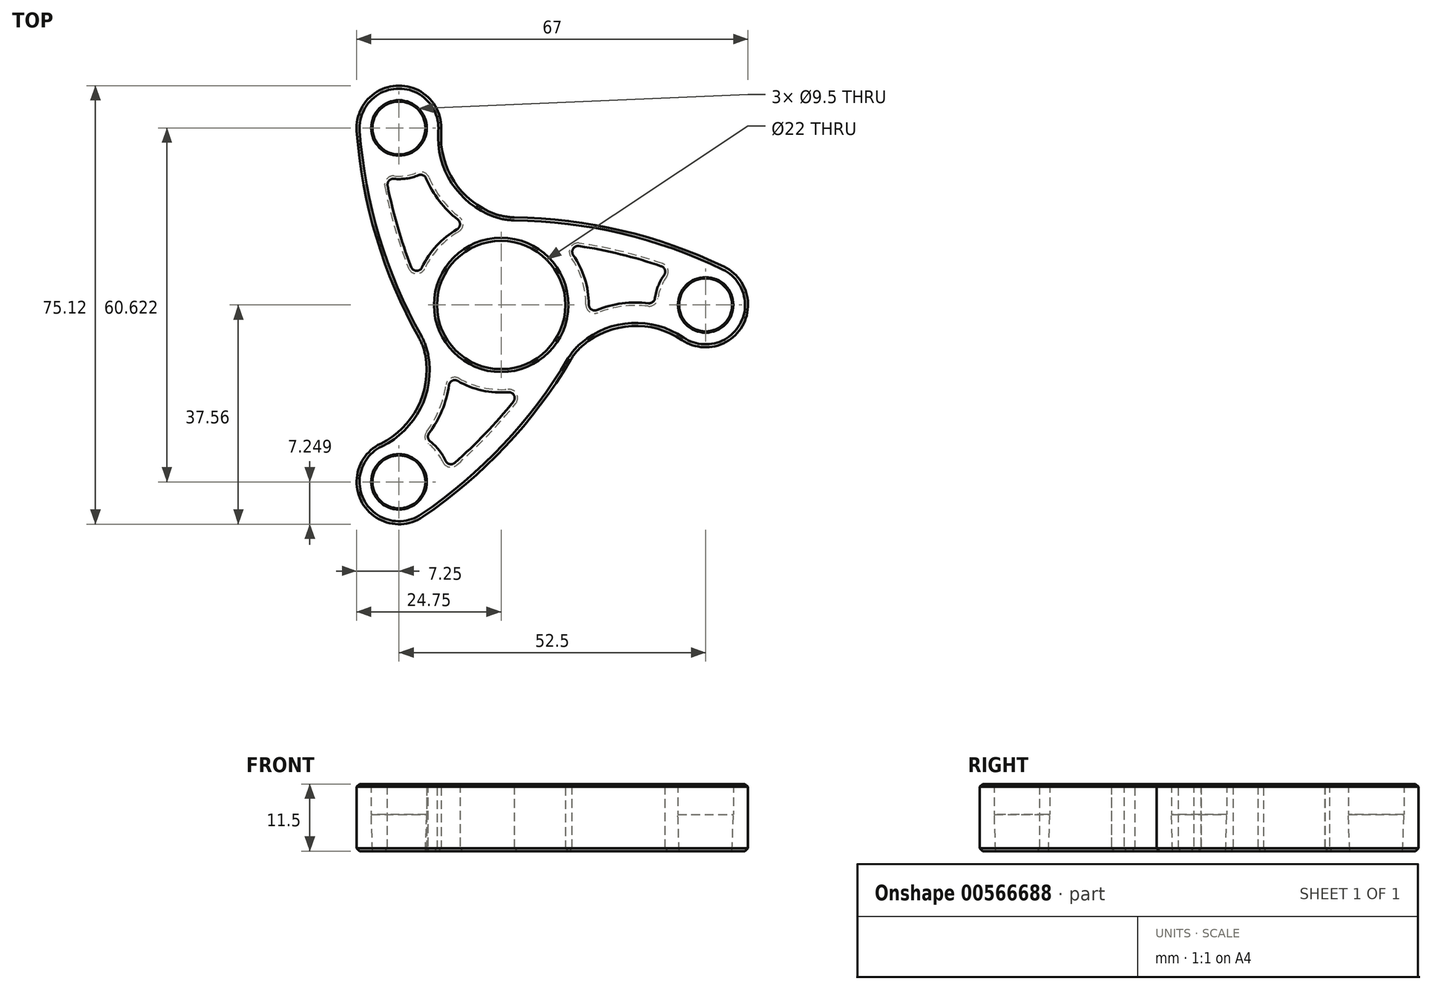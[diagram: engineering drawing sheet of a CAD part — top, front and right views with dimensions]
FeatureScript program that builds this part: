
annotation { "Feature Type Name" : "Feature", "Feature Type Description" : "" }
export const myFeature = defineFeature(function(context is Context, id is Id, definition is map)
    precondition{}
    {
        {
            var Q0;
            Q0=qCreatedBy(makeId("Top.planeOp"),FACE);
            var sketch = newSketch(context, id + "F0", { "sketchPlane" : qUnion([Q0])});
            skCircle(sketch, "E0", {"center": v(0, 0) * mm, "radius": 11 * mm});
            skArc(sketch, "E1.0", {"start": v(-0.24, 15) * mm, "mid": v(-13.39, -6.77) * mm, "end": v(11.93, -9.1) * mm});
            skLineSegment(sketch, "E2", {"start": v(0, 0) * mm, "end": v(35, 0) * mm, "construction": true});
            skArc(sketch, "E3", {"start": v(30.93, -6) * mm, "mid": v(41.28, -3.62) * mm, "end": v(38.16, 6.53) * mm});
            skArc(sketch, "E4", {"start": v(30.93, -6) * mm, "mid": v(20.81, -3.76) * mm, "end": v(11.93, -9.1) * mm});
            skArc(sketch, "E5", {"start": v(38.16, 6.53) * mm, "mid": v(19.45, 13.01) * mm, "end": v(-0.24, 15) * mm});
            skSolve(sketch);
        }
        {
            var Q0;
            Q0=makeQuery(id+"F0.imprint","IMPRINT",FACE,{"disambiguationData":[TD([[makeQuery(id+"F0.imprint","IMPRINT",EDGE,{"derivedFrom":sQuery(id+"F0.wireOp",EDGE,"E0")}),-1.0]])]});
            extrude(context, id + "F1", {"entities" : qUnion([Q0]), "endBound" : BoundingType.SYMMETRIC, "depth" : (9.5 + 2) * mm, "offsetDistance" : 25 * mm});
        }
        {
            var Q0;
            Q0=qCreatedBy(makeId("Front.planeOp"),FACE);
            var sketch = newSketch(context, id + "F2", { "sketchPlane" : qUnion([Q0])});
            skLineSegment(sketch, "E6", {"start": v(35, 5.95) * mm, "end": v(35, -6.38) * mm, "construction": true});
            skLineSegment(sketch, "E7", {"start": v(35, 5.75) * mm, "end": v(39.75, 5.75) * mm});
            skLineSegment(sketch, "E8", {"start": v(39.75, 5.75) * mm, "end": v(39.75, 0.5) * mm});
            skLineSegment(sketch, "E9", {"start": v(39.75, 0.5) * mm, "end": v(39.53, -5.75) * mm});
            skLineSegment(sketch, "E10", {"start": v(39.53, -5.75) * mm, "end": v(35, -5.75) * mm});
            skLineSegment(sketch, "E11", {"start": v(35, -5.75) * mm, "end": v(35, 5.75) * mm});
            skSolve(sketch);
        }
        {
            var Q0;
            Q0=qSketchRegion(id+"F2",true);
            var Q1;
            Q1=sQuery(id+"F2.wireOp",EDGE,"E6");
            revolve(context, id + "F3", {"operationType" : NewBodyOperationType.REMOVE, "entities" : qUnion([Q0]), "axis" : qUnion([Q1]), "revolveType" : RevolveType.FULL, "oppositeDirection" : true});
        }
        {
            var Q0;
            Q0=makeQuery(id+"F1.opExtrude","CAP_FACE",FACE,{"disambiguationData":[OSD([sQuery(id+"F0.wireOp",EDGE,"E0"),sQuery(id+"F0.wireOp",EDGE,"E1.0"),sQuery(id+"F0.wireOp",EDGE,"E3"),sQuery(id+"F0.wireOp",EDGE,"E4"),sQuery(id+"F0.wireOp",EDGE,"E5")])],"isStart":false});
            var sketch = newSketch(context, id + "F4", { "sketchPlane" : qUnion([Q0])});
            skArc(sketch, "E12.0", {"start": v(14.92, -1.53) * mm, "mid": v(20.45, 0.23) * mm, "end": v(26.25, 0.13) * mm});
            skArc(sketch, "E12.2", {"start": v(28.78, 6.15) * mm, "mid": v(19.9, 8.8) * mm, "end": v(10.78, 10.43) * mm});
            skArc(sketch, "E13.0", {"start": v(14.92, -1.53) * mm, "mid": v(14.17, 4.91) * mm, "end": v(10.78, 10.43) * mm});
            skArc(sketch, "E14.0", {"start": v(28.78, 6.15) * mm, "mid": v(26.93, 3.39) * mm, "end": v(26.25, 0.13) * mm});
            skSolve(sketch);
        }
        {
            var Q0;
            Q0=qSketchRegion(id+"F4",true);
            extrude(context, id + "F5", {"entities" : qUnion([Q0]), "operationType" : NewBodyOperationType.REMOVE, "oppositeDirection" : true, "depth" : 25 * mm, "offsetDistance" : 25 * mm});
        }
        {
            var Q0;
            Q0=makeQuery(id+"F5.boolean.opBoolean","COPY",EDGE,{"derivedFrom":makeQuery(id+"F5.opExtrude","SWEPT_EDGE",EDGE,{"disambiguationData":[OSD([sQuery(id+"F4.wireOp",EDGE,"E12.0"),sQuery(id+"F4.wireOp",EDGE,"E13.0")])]})});
            var Q1;
            Q1=makeQuery(id+"F5.boolean.opBoolean","COPY",EDGE,{"derivedFrom":makeQuery(id+"F5.opExtrude","SWEPT_EDGE",EDGE,{"disambiguationData":[OSD([sQuery(id+"F4.wireOp",EDGE,"E12.2"),sQuery(id+"F4.wireOp",EDGE,"E13.0")])]})});
            var Q2;
            Q2=makeQuery(id+"F5.boolean.opBoolean","COPY",EDGE,{"derivedFrom":makeQuery(id+"F5.opExtrude","SWEPT_EDGE",EDGE,{"disambiguationData":[OSD([sQuery(id+"F4.wireOp",EDGE,"E12.0"),sQuery(id+"F4.wireOp",EDGE,"E14.0")])]})});
            var Q3;
            Q3=makeQuery(id+"F5.boolean.opBoolean","COPY",EDGE,{"derivedFrom":makeQuery(id+"F5.opExtrude","SWEPT_EDGE",EDGE,{"disambiguationData":[OSD([sQuery(id+"F4.wireOp",EDGE,"E12.2"),sQuery(id+"F4.wireOp",EDGE,"E14.0")])]})});
            fillet(context, id + "F6", {"entities" : qUnion([Q0, Q1, Q2, Q3]), "radius" : 1 * mm, "tangentPropagation" : true, "allowEdgeOverflow" : false});
        }
        {
            var Q0;
            Q0=makeQuery(id+"F5.boolean.opBoolean","COPY",EDGE,{"derivedFrom":makeQuery(id+"F5.opExtrude","CAP_EDGE",EDGE,{"disambiguationData":[OSD([sQuery(id+"F4.wireOp",EDGE,"E12.0")])],"isStart":true})});
            var Q1;
            Q1=makeQuery(id+"F5.boolean.opBoolean","COPY",EDGE,{"derivedFrom":makeQuery(id+"F5.opExtrude","CAP_EDGE",EDGE,{"disambiguationData":[OSD([sQuery(id+"F4.wireOp",EDGE,"E13.0")])],"isStart":true})});
            var Q2;
            Q2=makeQuery(id+"F5.boolean.opBoolean","COPY",EDGE,{"derivedFrom":makeQuery(id+"F5.opExtrude","CAP_EDGE",EDGE,{"disambiguationData":[OSD([sQuery(id+"F4.wireOp",EDGE,"E12.2")])],"isStart":true})});
            var Q3;
            Q3=makeQuery(id+"F5.boolean.opBoolean","COPY",EDGE,{"derivedFrom":makeQuery(id+"F5.opExtrude","CAP_EDGE",EDGE,{"disambiguationData":[OSD([sQuery(id+"F4.wireOp",EDGE,"E14.0")])],"isStart":true})});
            var Q4;
            Q4=makeQuery(id+"F1.opExtrude","CAP_EDGE",EDGE,{"disambiguationData":[OSD([sQuery(id+"F0.wireOp",EDGE,"E0")])],"isStart":false});
            var Q5;
            Q5=makeQuery(id+"F5.boolean.opBoolean","INTERSECT",EDGE,{"derivedFrom":[makeQuery(id+"F1.opExtrude","CAP_FACE",FACE,{"disambiguationData":[OSD([sQuery(id+"F0.wireOp",EDGE,"E0"),sQuery(id+"F0.wireOp",EDGE,"E1.0"),sQuery(id+"F0.wireOp",EDGE,"E3"),sQuery(id+"F0.wireOp",EDGE,"E4"),sQuery(id+"F0.wireOp",EDGE,"E5")])],"isStart":true}),makeQuery(id+"F5.opExtrude","SWEPT_FACE",FACE,{"disambiguationData":[OSD([sQuery(id+"F4.wireOp",EDGE,"E12.2")])]})]});
            var Q6;
            Q6=makeQuery(id+"F5.boolean.opBoolean","INTERSECT",EDGE,{"derivedFrom":[makeQuery(id+"F1.opExtrude","CAP_FACE",FACE,{"disambiguationData":[OSD([sQuery(id+"F0.wireOp",EDGE,"E0"),sQuery(id+"F0.wireOp",EDGE,"E1.0"),sQuery(id+"F0.wireOp",EDGE,"E3"),sQuery(id+"F0.wireOp",EDGE,"E4"),sQuery(id+"F0.wireOp",EDGE,"E5")])],"isStart":true}),makeQuery(id+"F5.opExtrude","SWEPT_FACE",FACE,{"disambiguationData":[OSD([sQuery(id+"F4.wireOp",EDGE,"E12.0")])]})]});
            var Q7;
            Q7=makeQuery(id+"F5.boolean.opBoolean","INTERSECT",EDGE,{"derivedFrom":[makeQuery(id+"F1.opExtrude","CAP_FACE",FACE,{"disambiguationData":[OSD([sQuery(id+"F0.wireOp",EDGE,"E0"),sQuery(id+"F0.wireOp",EDGE,"E1.0"),sQuery(id+"F0.wireOp",EDGE,"E3"),sQuery(id+"F0.wireOp",EDGE,"E4"),sQuery(id+"F0.wireOp",EDGE,"E5")])],"isStart":true}),makeQuery(id+"F5.opExtrude","SWEPT_FACE",FACE,{"disambiguationData":[OSD([sQuery(id+"F4.wireOp",EDGE,"E14.0")])]})]});
            var Q8;
            Q8=makeQuery(id+"F1.opExtrude","CAP_EDGE",EDGE,{"disambiguationData":[OSD([sQuery(id+"F0.wireOp",EDGE,"E0")])],"isStart":true});
            var Q9;
            Q9=makeQuery(id+"F5.boolean.opBoolean","INTERSECT",EDGE,{"derivedFrom":[makeQuery(id+"F1.opExtrude","CAP_FACE",FACE,{"disambiguationData":[OSD([sQuery(id+"F0.wireOp",EDGE,"E0"),sQuery(id+"F0.wireOp",EDGE,"E1.0"),sQuery(id+"F0.wireOp",EDGE,"E3"),sQuery(id+"F0.wireOp",EDGE,"E4"),sQuery(id+"F0.wireOp",EDGE,"E5")])],"isStart":true}),makeQuery(id+"F5.opExtrude","SWEPT_FACE",FACE,{"disambiguationData":[OSD([sQuery(id+"F4.wireOp",EDGE,"E13.0")])]})]});
            var Q10;
            Q10=makeQuery(id+"F3.boolean.opBoolean","COPY",EDGE,{"derivedFrom":makeQuery(id+"F3.opRevolve","SWEPT_EDGE",EDGE,{"disambiguationData":[OSD([sQuery(id+"F2.wireOp",EDGE,"E7"),sQuery(id+"F2.wireOp",EDGE,"E8")])]})});
            chamfer(context, id + "F7", {"entities" : qUnion([Q0, Q1, Q2, Q3, Q4, Q5, Q6, Q7, Q8, Q9, Q10]), "width" : .5 * mm, "tangentPropagation" : true});
        }
        {
            var Q0;
            Q0=makeQuery(id+"F1.opExtrude","SWEPT_BODY",BODY,{"disambiguationData":[OSD([sQuery(id+"F0.wireOp",EDGE,"E0"),sQuery(id+"F0.wireOp",EDGE,"E1.0"),sQuery(id+"F0.wireOp",EDGE,"E3"),sQuery(id+"F0.wireOp",EDGE,"E4"),sQuery(id+"F0.wireOp",EDGE,"E5")])]});
            var Q1;
            Q1=makeQuery(id+"F1.opExtrude","SWEPT_FACE",FACE,{"disambiguationData":[OSD([sQuery(id+"F0.wireOp",EDGE,"E0")])]});
            circularPattern(context, id + "F8", {"operationType" : NewBodyOperationType.ADD, "entities" : qUnion([Q0]), "axis" : qUnion([Q1]), "angle" : 360 * degree, "instanceCount" : 3, "equalSpace" : true});
        }
        {
            var Q0;
            Q0=makeQuery(id+"F8.boolean.opBoolean","INTERSECT",EDGE,{"derivedFrom":[makeQuery(id+"F1.opExtrude","SWEPT_FACE",FACE,{"disambiguationData":[OSD([sQuery(id+"F0.wireOp",EDGE,"E4")])]}),makeQuery(id+"F8.opPattern","COPY",FACE,{"derivedFrom":makeQuery(id+"F1.opExtrude","SWEPT_FACE",FACE,{"disambiguationData":[OSD([sQuery(id+"F0.wireOp",EDGE,"E5")])]}),"instanceName":"2"})]});
            var Q1;
            Q1=makeQuery(id+"F8.boolean.opBoolean","INTERSECT",EDGE,{"derivedFrom":[makeQuery(id+"F1.opExtrude","SWEPT_FACE",FACE,{"disambiguationData":[OSD([sQuery(id+"F0.wireOp",EDGE,"E5")])]}),makeQuery(id+"F8.opPattern","COPY",FACE,{"derivedFrom":makeQuery(id+"F1.opExtrude","SWEPT_FACE",FACE,{"disambiguationData":[OSD([sQuery(id+"F0.wireOp",EDGE,"E4")])]}),"instanceName":"1"})]});
            var Q2;
            Q2=makeQuery(id+"F8.boolean.opBoolean","INTERSECT",EDGE,{"derivedFrom":[makeQuery(id+"F8.opPattern","COPY",FACE,{"derivedFrom":makeQuery(id+"F1.opExtrude","SWEPT_FACE",FACE,{"disambiguationData":[OSD([sQuery(id+"F0.wireOp",EDGE,"E5")])]}),"instanceName":"1"}),makeQuery(id+"F8.opPattern","COPY",FACE,{"derivedFrom":makeQuery(id+"F1.opExtrude","SWEPT_FACE",FACE,{"disambiguationData":[OSD([sQuery(id+"F0.wireOp",EDGE,"E4")])]}),"instanceName":"2"})]});
            fillet(context, id + "F9", {"entities" : qUnion([Q0, Q1, Q2]), "radius" : 10 * mm, "tangentPropagation" : true, "allowEdgeOverflow" : false});
        }
        {
            var Q0;
            Q0=makeQuery(id+"F1.opExtrude","CAP_EDGE",EDGE,{"disambiguationData":[OSD([sQuery(id+"F0.wireOp",EDGE,"E5")])],"isStart":false});
            var Q1;
            Q1=makeQuery(id+"F1.opExtrude","CAP_EDGE",EDGE,{"disambiguationData":[OSD([sQuery(id+"F0.wireOp",EDGE,"E5")])],"isStart":true});
            var Q2;
            Q2=makeQuery(id+"F8.opPattern","COPY",EDGE,{"derivedFrom":makeQuery(id+"F1.opExtrude","CAP_EDGE",EDGE,{"disambiguationData":[OSD([sQuery(id+"F0.wireOp",EDGE,"E1.0")])],"isStart":false}),"instanceName":"1"});
            var Q3;
            {var subQ0=sQuery(id+"F0.wireOp",EDGE,"E5");var subQ1=sQuery(id+"F0.wireOp",EDGE,"E4");var subQ2=sQuery(id+"F0.wireOp",EDGE,"E3");var subQ3=sQuery(id+"F0.wireOp",EDGE,"E1.0");var subQ4=sQuery(id+"F0.wireOp",EDGE,"E0");var subQ5=makeQuery(id+"F1.opExtrude","CAP_FACE",FACE,{"disambiguationData":[OSD([subQ4,subQ3,subQ2,subQ1,subQ0])],"isStart":false});var subQ6=subQ5;var subQ7=sQuery(id+"F4.wireOp",EDGE,"E13.0");var subQ8=sQuery(id+"F4.wireOp",EDGE,"E12.0");Q3=makeQuery(id+"F8.boolean.opBoolean","SPLIT",EDGE,{"disambiguationData":[TD([makeQuery(id+"F8.opPattern","COPY",FACE,{"derivedFrom":makeQuery(id+"F7.opChamfer","BLEND_FACE",FACE,{"disambiguationData":[OSD([subQ4,subQ3,subQ2,subQ1,subQ0,subQ8,subQ7]),TDD([makeQuery(id+"F6.opFillet","BLEND_EDGE",EDGE,{"blendedFrom":[makeQuery(id+"F5.boolean.opBoolean","COPY",EDGE,{"derivedFrom":makeQuery(id+"F5.opExtrude","SWEPT_EDGE",EDGE,{"disambiguationData":[OSD([subQ8,subQ7])]})}),subQ6],"blendedInto":[subQ6]})])]}),"instanceName":"2"})])],"derivedFrom":makeQuery(id+"F1.opExtrude","CAP_EDGE",EDGE,{"disambiguationData":[OSD([subQ3])],"isStart":false})});}
            var Q4;
            {var subQ0=sQuery(id+"F0.wireOp",EDGE,"E5");var subQ1=sQuery(id+"F0.wireOp",EDGE,"E4");var subQ2=sQuery(id+"F0.wireOp",EDGE,"E3");var subQ3=sQuery(id+"F0.wireOp",EDGE,"E1.0");var subQ4=sQuery(id+"F0.wireOp",EDGE,"E0");var subQ5=makeQuery(id+"F1.opExtrude","CAP_FACE",FACE,{"disambiguationData":[OSD([subQ4,subQ3,subQ2,subQ1,subQ0])],"isStart":false});var subQ6=subQ5;var subQ7=sQuery(id+"F4.wireOp",EDGE,"E13.0");var subQ9=sQuery(id+"F4.wireOp",EDGE,"E12.0");Q4=makeQuery(id+"F8.boolean.opBoolean","SPLIT",EDGE,{"disambiguationData":[TD([makeQuery(id+"F8.opPattern","COPY",FACE,{"derivedFrom":makeQuery(id+"F7.opChamfer","BLEND_FACE",FACE,{"disambiguationData":[OSD([subQ4,subQ3,subQ2,subQ1,subQ0,subQ9,subQ7]),TDD([makeQuery(id+"F6.opFillet","BLEND_EDGE",EDGE,{"blendedFrom":[makeQuery(id+"F5.boolean.opBoolean","COPY",EDGE,{"derivedFrom":makeQuery(id+"F5.opExtrude","SWEPT_EDGE",EDGE,{"disambiguationData":[OSD([subQ9,subQ7])]})}),subQ6],"blendedInto":[subQ6]})])]}),"instanceName":"1"})])],"derivedFrom":makeQuery(id+"F1.opExtrude","CAP_EDGE",EDGE,{"disambiguationData":[OSD([subQ3])],"isStart":false})});}
            var Q5;
            {var subQ0=sQuery(id+"F0.wireOp",EDGE,"E5");var subQ1=sQuery(id+"F0.wireOp",EDGE,"E4");var subQ2=sQuery(id+"F0.wireOp",EDGE,"E3");var subQ3=sQuery(id+"F0.wireOp",EDGE,"E1.0");var subQ4=sQuery(id+"F0.wireOp",EDGE,"E0");var subQ5=makeQuery(id+"F1.opExtrude","CAP_FACE",FACE,{"disambiguationData":[OSD([subQ4,subQ3,subQ2,subQ1,subQ0])],"isStart":true});var subQ6=subQ5;var subQ7=sQuery(id+"F4.wireOp",EDGE,"E13.0");var subQ8=sQuery(id+"F4.wireOp",EDGE,"E12.0");Q5=makeQuery(id+"F8.boolean.opBoolean","SPLIT",EDGE,{"disambiguationData":[TD([makeQuery(id+"F8.opPattern","COPY",FACE,{"derivedFrom":makeQuery(id+"F7.opChamfer","BLEND_FACE",FACE,{"disambiguationData":[OSD([subQ4,subQ3,subQ2,subQ1,subQ0,subQ8,subQ7]),TDD([makeQuery(id+"F6.opFillet","BLEND_EDGE",EDGE,{"blendedFrom":[makeQuery(id+"F5.boolean.opBoolean","COPY",EDGE,{"derivedFrom":makeQuery(id+"F5.opExtrude","SWEPT_EDGE",EDGE,{"disambiguationData":[OSD([subQ8,subQ7])]})}),subQ6],"blendedInto":[subQ6]})])]}),"instanceName":"2"})])],"derivedFrom":makeQuery(id+"F1.opExtrude","CAP_EDGE",EDGE,{"disambiguationData":[OSD([subQ3])],"isStart":true})});}
            var Q6;
            {var subQ0=sQuery(id+"F0.wireOp",EDGE,"E5");var subQ1=sQuery(id+"F0.wireOp",EDGE,"E4");var subQ2=sQuery(id+"F0.wireOp",EDGE,"E3");var subQ3=sQuery(id+"F0.wireOp",EDGE,"E1.0");var subQ4=sQuery(id+"F0.wireOp",EDGE,"E0");var subQ5=makeQuery(id+"F1.opExtrude","CAP_FACE",FACE,{"disambiguationData":[OSD([subQ4,subQ3,subQ2,subQ1,subQ0])],"isStart":true});var subQ6=subQ5;var subQ7=sQuery(id+"F4.wireOp",EDGE,"E13.0");var subQ9=sQuery(id+"F4.wireOp",EDGE,"E12.0");Q6=makeQuery(id+"F8.boolean.opBoolean","SPLIT",EDGE,{"disambiguationData":[TD([makeQuery(id+"F8.opPattern","COPY",FACE,{"derivedFrom":makeQuery(id+"F7.opChamfer","BLEND_FACE",FACE,{"disambiguationData":[OSD([subQ4,subQ3,subQ2,subQ1,subQ0,subQ9,subQ7]),TDD([makeQuery(id+"F6.opFillet","BLEND_EDGE",EDGE,{"blendedFrom":[makeQuery(id+"F5.boolean.opBoolean","COPY",EDGE,{"derivedFrom":makeQuery(id+"F5.opExtrude","SWEPT_EDGE",EDGE,{"disambiguationData":[OSD([subQ9,subQ7])]})}),subQ6],"blendedInto":[subQ6]})])]}),"instanceName":"1"})])],"derivedFrom":makeQuery(id+"F1.opExtrude","CAP_EDGE",EDGE,{"disambiguationData":[OSD([subQ3])],"isStart":true})});}
            var Q7;
            Q7=makeQuery(id+"F8.opPattern","COPY",EDGE,{"derivedFrom":makeQuery(id+"F1.opExtrude","CAP_EDGE",EDGE,{"disambiguationData":[OSD([sQuery(id+"F0.wireOp",EDGE,"E1.0")])],"isStart":true}),"instanceName":"1"});
            var Q8;
            Q8=makeQuery(id+"F3.boolean.opBoolean","COPY",EDGE,{"derivedFrom":makeQuery(id+"F3.opRevolve","SWEPT_EDGE",EDGE,{"disambiguationData":[OSD([sQuery(id+"F2.wireOp",EDGE,"E9"),sQuery(id+"F2.wireOp",EDGE,"E10")])]})});
            var Q9;
            Q9=makeQuery(id+"F8.opPattern","COPY",EDGE,{"derivedFrom":makeQuery(id+"F3.boolean.opBoolean","COPY",EDGE,{"derivedFrom":makeQuery(id+"F3.opRevolve","SWEPT_EDGE",EDGE,{"disambiguationData":[OSD([sQuery(id+"F2.wireOp",EDGE,"E9"),sQuery(id+"F2.wireOp",EDGE,"E10")])]})}),"instanceName":"2"});
            var Q10;
            Q10=makeQuery(id+"F8.opPattern","COPY",EDGE,{"derivedFrom":makeQuery(id+"F3.boolean.opBoolean","COPY",EDGE,{"derivedFrom":makeQuery(id+"F3.opRevolve","SWEPT_EDGE",EDGE,{"disambiguationData":[OSD([sQuery(id+"F2.wireOp",EDGE,"E9"),sQuery(id+"F2.wireOp",EDGE,"E10")])]})}),"instanceName":"1"});
            chamfer(context, id + "F10", {"entities" : qUnion([Q0, Q1, Q2, Q3, Q4, Q5, Q6, Q7, Q8, Q9, Q10]), "width" : .5 * mm, "tangentPropagation" : true});
        }
    });
